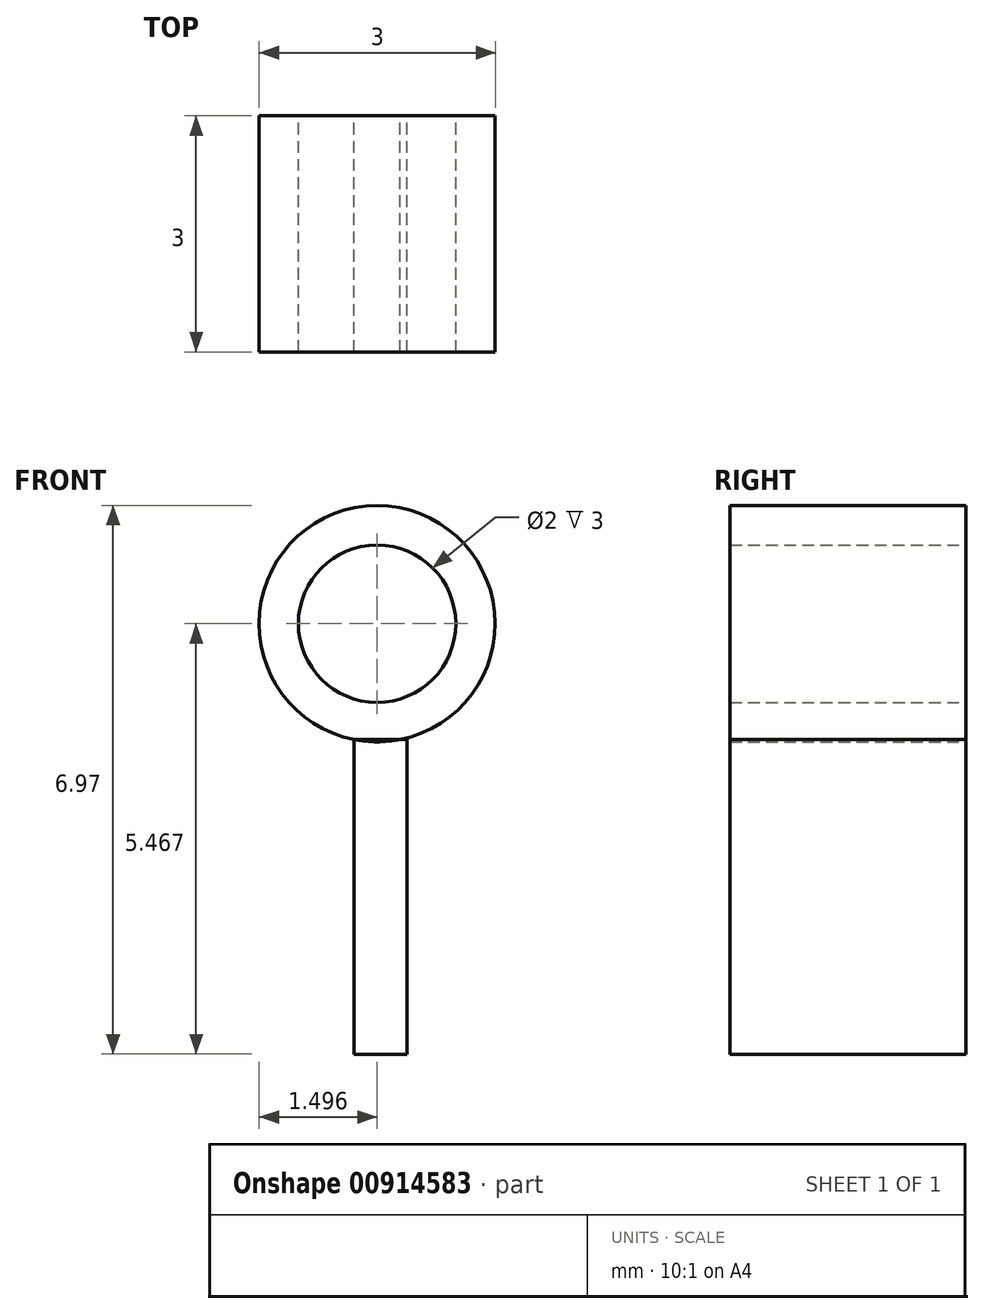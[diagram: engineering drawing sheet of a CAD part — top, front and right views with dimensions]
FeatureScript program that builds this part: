
annotation { "Feature Type Name" : "Feature", "Feature Type Description" : "" }
export const myFeature = defineFeature(function(context is Context, id is Id, definition is map)
    precondition{}
    {
        {
            var Q0;
            Q0=qCreatedBy(makeId("Front.planeOp"),FACE);
            var sketch = newSketch(context, id + "F0", { "sketchPlane" : qUnion([Q0])});
            skCircle(sketch, "E0", {"center": v(-43, 31.1) * mm, "radius": 1 * mm});
            skCircle(sketch, "E1", {"center": v(-43, 31.1) * mm, "radius": 1.5 * mm});
            skLineSegment(sketch, "E2.bottom", {"start": v(-43.3, 29.63) * mm, "end": v(-42.62, 29.63) * mm});
            skLineSegment(sketch, "E2.top", {"start": v(-43.3, 25.63) * mm, "end": v(-42.62, 25.63) * mm});
            skLineSegment(sketch, "E2.left", {"start": v(-43.3, 29.63) * mm, "end": v(-43.3, 25.63) * mm});
            skLineSegment(sketch, "E2.right", {"start": v(-42.62, 29.63) * mm, "end": v(-42.62, 25.63) * mm});
            skSolve(sketch);
        }
        {
            var Q0;
            Q0=makeQuery(id+"F0.imprint","IMPRINT",FACE,{"disambiguationData":[TD([[makeQuery(id+"F0.imprint","IMPRINT",EDGE,{"derivedFrom":sQuery(id+"F0.wireOp",EDGE,"E2.top")}),1.0]])]});
            var Q1;
            Q1=makeQuery(id+"F0.imprint","IMPRINT",FACE,{"disambiguationData":[TD([[makeQuery(id+"F0.imprint","IMPRINT",EDGE,{"derivedFrom":sQuery(id+"F0.wireOp",EDGE,"E0")}),-1.0]])]});
            extrude(context, id + "F1", {"entities" : qUnion([Q0, Q1]), "depth" : 3 * mm, "offsetDistance" : 25.4 * mm});
        }
    });
